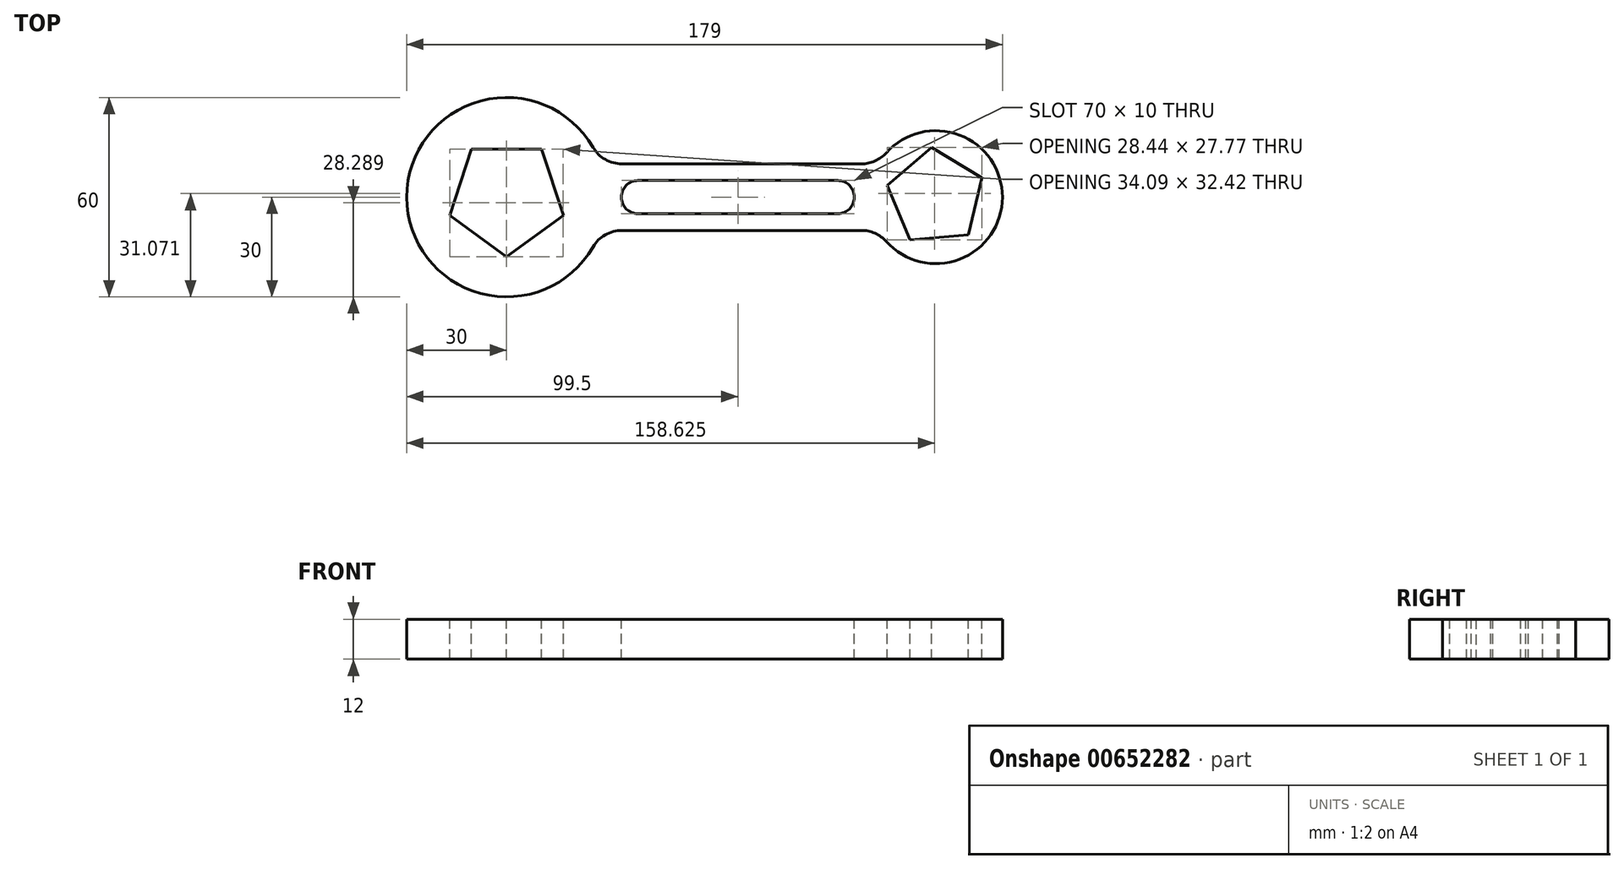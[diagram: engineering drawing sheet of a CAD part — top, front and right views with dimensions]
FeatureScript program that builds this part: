
annotation { "Feature Type Name" : "Feature", "Feature Type Description" : "" }
export const myFeature = defineFeature(function(context is Context, id is Id, definition is map)
    precondition{}
    {
        {
            var Q0;
            Q0=qCreatedBy(makeId("Top.planeOp"),FACE);
            var sketch = newSketch(context, id + "F0", { "sketchPlane" : qUnion([Q0])});
            skLineSegment(sketch, "E0.bottom", {"start": v(64.5, -10) * mm, "end": v(-64.5, -10) * mm});
            skLineSegment(sketch, "E0.top", {"start": v(64.5, 10) * mm, "end": v(-64.5, 10) * mm});
            skLineSegment(sketch, "E0.left", {"start": v(64.5, -10) * mm, "end": v(64.5, 10) * mm});
            skLineSegment(sketch, "E0.right", {"start": v(-64.5, -10) * mm, "end": v(-64.5, 10) * mm});
            skPoint(sketch, "E0.middle", {"position": v(0, 0) * mm});
            skCircle(sketch, "E1", {"center": v(64.5, 0) * mm, "radius": 20 * mm});
            skCircle(sketch, "E2", {"center": v(-64.5, 0) * mm, "radius": 30 * mm});
            skSolve(sketch);
        }
        {
            var Q0;
            {var subQ0=sQuery(id+"F0.wireOp",EDGE,"E0.right");Q0=makeQuery(id+"F0.imprint","IMPRINT",FACE,{"disambiguationData":[TD([[makeQuery(id+"F0.imprint","IMPRINT",EDGE,{"derivedFrom":subQ0}),1.0]])]});}
            var Q1;
            {var subQ0=sQuery(id+"F0.wireOp",EDGE,"E1");var subQ1=sQuery(id+"F0.wireOp",EDGE,"E0.bottom");var subQ2=makeQuery(id+"F0.imprint","INTERSECT",VERTEX,{"derivedFrom":[subQ1,subQ0]});Q1=makeQuery(id+"F0.imprint","IMPRINT",FACE,{"disambiguationData":[TD([[makeQuery(id+"F0.imprint","IMPRINT",EDGE,{"disambiguationData":[TD([[subQ2,-1.0]])],"derivedFrom":subQ1}),-1.0]])]});}
            var Q2;
            {var subQ0=sQuery(id+"F0.wireOp",EDGE,"E0.right");Q2=makeQuery(id+"F0.imprint","IMPRINT",FACE,{"disambiguationData":[TD([[makeQuery(id+"F0.imprint","IMPRINT",EDGE,{"derivedFrom":subQ0}),-1.0]])]});}
            var Q3;
            {var subQ0=sQuery(id+"F0.wireOp",EDGE,"E0.left");Q3=makeQuery(id+"F0.imprint","IMPRINT",FACE,{"disambiguationData":[TD([[makeQuery(id+"F0.imprint","IMPRINT",EDGE,{"derivedFrom":subQ0}),1.0]])]});}
            var Q4;
            {var subQ0=sQuery(id+"F0.wireOp",EDGE,"E0.left");Q4=makeQuery(id+"F0.imprint","IMPRINT",FACE,{"disambiguationData":[TD([[makeQuery(id+"F0.imprint","IMPRINT",EDGE,{"derivedFrom":subQ0}),-1.0]])]});}
            extrude(context, id + "F1", {"entities" : qUnion([Q0, Q1, Q2, Q3, Q4]), "depth" : 12 * mm, "offsetDistance" : 25 * mm});
        }
        {
            var Q0;
            Q0=makeQuery(id+"F1.opExtrude","CAP_FACE",FACE,{"disambiguationData":[OSD([sQuery(id+"F0.wireOp",EDGE,"E0.bottom"),sQuery(id+"F0.wireOp",EDGE,"E0.top"),sQuery(id+"F0.wireOp",EDGE,"E1"),sQuery(id+"F0.wireOp",EDGE,"E2")])],"isStart":false});
            var sketch = newSketch(context, id + "F2", { "sketchPlane" : qUnion([Q0])});
            skCircle(sketch, "E3.cCircle", {"center": v(-64.5, 0) * mm, "radius": 17.92 * mm, "construction": true});
            skLineSegment(sketch, "E3.0", {"start": v(-47.46, -5.54) * mm, "end": v(-64.5, -17.92) * mm});
            skLineSegment(sketch, "E3.1", {"start": v(-64.5, -17.92) * mm, "end": v(-81.54, -5.54) * mm});
            skLineSegment(sketch, "E3.2", {"start": v(-81.54, -5.54) * mm, "end": v(-75.03, 14.5) * mm});
            skLineSegment(sketch, "E3.3", {"start": v(-75.03, 14.5) * mm, "end": v(-53.97, 14.5) * mm});
            skLineSegment(sketch, "E3.4", {"start": v(-53.97, 14.5) * mm, "end": v(-47.46, -5.54) * mm});
            skCircle(sketch, "E4.cCircle", {"center": v(64.5, 0) * mm, "radius": 15 * mm, "construction": true});
            skLineSegment(sketch, "E4.0", {"start": v(74.27, -11.38) * mm, "end": v(56.7, -12.81) * mm});
            skLineSegment(sketch, "E4.1", {"start": v(56.7, -12.81) * mm, "end": v(49.9, 3.47) * mm});
            skLineSegment(sketch, "E4.2", {"start": v(49.9, 3.47) * mm, "end": v(63.28, 14.95) * mm});
            skLineSegment(sketch, "E4.3", {"start": v(63.28, 14.95) * mm, "end": v(78.35, 5.78) * mm});
            skLineSegment(sketch, "E4.4", {"start": v(78.35, 5.78) * mm, "end": v(74.27, -11.38) * mm});
            skSolve(sketch);
        }
        {
            var Q0;
            Q0=makeQuery(id+"F2.imprint","IMPRINT",FACE,{"disambiguationData":[TD([[makeQuery(id+"F2.imprint","IMPRINT",EDGE,{"derivedFrom":sQuery(id+"F2.wireOp",EDGE,"E3.0")}),-1.0]])]});
            var Q1;
            Q1=makeQuery(id+"F2.imprint","IMPRINT",FACE,{"disambiguationData":[TD([[makeQuery(id+"F2.imprint","IMPRINT",EDGE,{"derivedFrom":sQuery(id+"F2.wireOp",EDGE,"E4.0")}),-1.0]])]});
            extrude(context, id + "F3", {"entities" : qUnion([Q0, Q1]), "operationType" : NewBodyOperationType.REMOVE, "oppositeDirection" : true, "depth" : 12 * mm, "offsetDistance" : 25 * mm});
        }
        {
            var Q0;
            Q0=makeQuery(id+"F1.opExtrude","CAP_FACE",FACE,{"disambiguationData":[OSD([sQuery(id+"F0.wireOp",EDGE,"E0.bottom"),sQuery(id+"F0.wireOp",EDGE,"E0.top"),sQuery(id+"F0.wireOp",EDGE,"E1"),sQuery(id+"F0.wireOp",EDGE,"E2")])],"isStart":false});
            var sketch = newSketch(context, id + "F4", { "sketchPlane" : qUnion([Q0])});
            skLineSegment(sketch, "E5.bottom", {"start": v(35, -5) * mm, "end": v(-25, -5) * mm});
            skLineSegment(sketch, "E5.top", {"start": v(35, 5) * mm, "end": v(-25, 5) * mm});
            skLineSegment(sketch, "E5.left", {"start": v(35, -5) * mm, "end": v(35, 5) * mm});
            skLineSegment(sketch, "E5.right", {"start": v(-25, -5) * mm, "end": v(-25, 5) * mm});
            skPoint(sketch, "E5.middle", {"position": v(0, 0) * mm});
            skCircle(sketch, "E6", {"center": v(-25, 0) * mm, "radius": 5 * mm});
            skCircle(sketch, "E7", {"center": v(35, 0) * mm, "radius": 5 * mm});
            skSolve(sketch);
        }
        {
            var Q0;
            {var subQ0=sQuery(id+"F4.wireOp",EDGE,"E5.right");Q0=makeQuery(id+"F4.imprint","IMPRINT",FACE,{"disambiguationData":[TD([[makeQuery(id+"F4.imprint","IMPRINT",EDGE,{"derivedFrom":subQ0}),1.0]])]});}
            var Q1;
            {var subQ0=sQuery(id+"F4.wireOp",EDGE,"E5.right");Q1=makeQuery(id+"F4.imprint","IMPRINT",FACE,{"disambiguationData":[TD([[makeQuery(id+"F4.imprint","IMPRINT",EDGE,{"derivedFrom":subQ0}),-1.0]])]});}
            var Q2;
            {var subQ0=sQuery(id+"F4.wireOp",EDGE,"E5.bottom");Q2=makeQuery(id+"F4.imprint","IMPRINT",FACE,{"disambiguationData":[TD([[makeQuery(id+"F4.imprint","IMPRINT",EDGE,{"derivedFrom":subQ0}),-1.0]])]});}
            var Q3;
            {var subQ0=sQuery(id+"F4.wireOp",EDGE,"E5.left");Q3=makeQuery(id+"F4.imprint","IMPRINT",FACE,{"disambiguationData":[TD([[makeQuery(id+"F4.imprint","IMPRINT",EDGE,{"derivedFrom":subQ0}),1.0]])]});}
            var Q4;
            {var subQ0=sQuery(id+"F4.wireOp",EDGE,"E5.left");Q4=makeQuery(id+"F4.imprint","IMPRINT",FACE,{"disambiguationData":[TD([[makeQuery(id+"F4.imprint","IMPRINT",EDGE,{"derivedFrom":subQ0}),-1.0]])]});}
            var Q5;
            Q5=makeQuery(id+"F1.opExtrude","CAP_FACE",FACE,{"disambiguationData":[OSD([sQuery(id+"F0.wireOp",EDGE,"E0.bottom"),sQuery(id+"F0.wireOp",EDGE,"E0.top"),sQuery(id+"F0.wireOp",EDGE,"E1"),sQuery(id+"F0.wireOp",EDGE,"E2")])],"isStart":true});
            extrude(context, id + "F5", {"entities" : qUnion([Q0, Q1, Q2, Q3, Q4]), "operationType" : NewBodyOperationType.REMOVE, "endBound" : BoundingType.UP_TO_SURFACE, "oppositeDirection" : true, "depth" : 12 * mm, "endBoundEntityFace" : qUnion([Q5]), "offsetDistance" : 25 * mm});
        }
        {
            var Q0;
            Q0=makeQuery(id+"F1.opExtrude","SWEPT_EDGE",EDGE,{"disambiguationData":[OSD([sQuery(id+"F0.wireOp",EDGE,"E0.bottom"),sQuery(id+"F0.wireOp",EDGE,"E2")])]});
            var Q1;
            Q1=makeQuery(id+"F1.opExtrude","SWEPT_EDGE",EDGE,{"disambiguationData":[OSD([sQuery(id+"F0.wireOp",EDGE,"E0.bottom"),sQuery(id+"F0.wireOp",EDGE,"E1")])]});
            var Q2;
            Q2=makeQuery(id+"F1.opExtrude","SWEPT_EDGE",EDGE,{"disambiguationData":[OSD([sQuery(id+"F0.wireOp",EDGE,"E0.top"),sQuery(id+"F0.wireOp",EDGE,"E2")])]});
            var Q3;
            Q3=makeQuery(id+"F1.opExtrude","SWEPT_EDGE",EDGE,{"disambiguationData":[OSD([sQuery(id+"F0.wireOp",EDGE,"E0.top"),sQuery(id+"F0.wireOp",EDGE,"E1")])]});
            fillet(context, id + "F6", {"entities" : qUnion([Q0, Q1, Q2, Q3]), "radius" : 10 * mm, "tangentPropagation" : true, "allowEdgeOverflow" : false});
        }
    });
